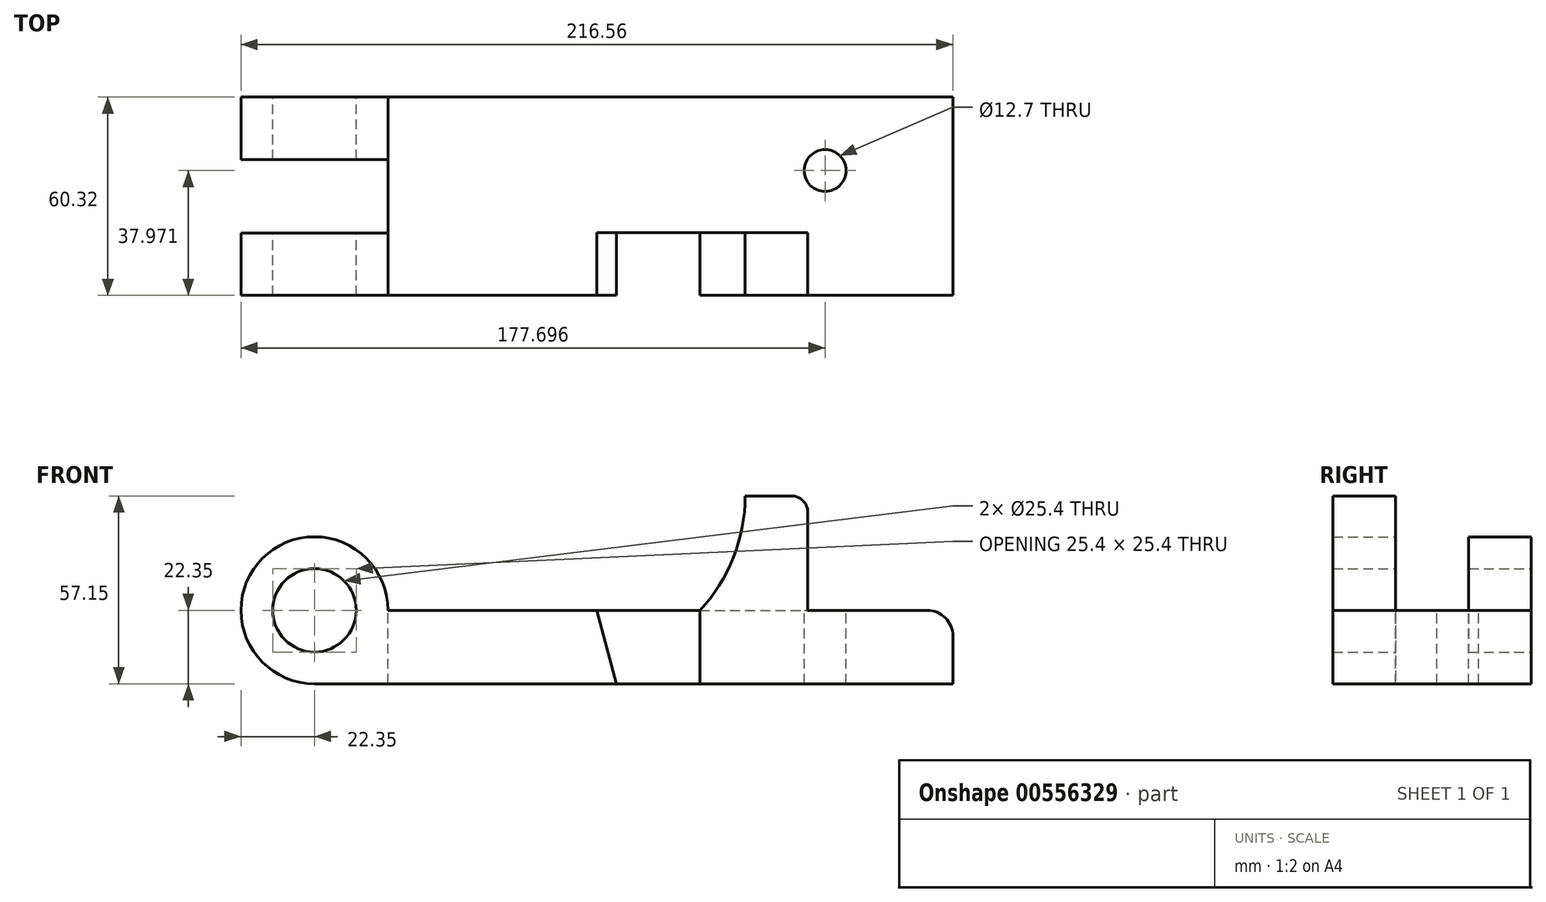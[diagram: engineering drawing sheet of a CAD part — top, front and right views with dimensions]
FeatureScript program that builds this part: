
annotation { "Feature Type Name" : "Feature", "Feature Type Description" : "" }
export const myFeature = defineFeature(function(context is Context, id is Id, definition is map)
    precondition{}
    {
        {
            var Q0;
            Q0=qCreatedBy(makeId("Front.planeOp"),FACE);
            var sketch = newSketch(context, id + "F0", { "sketchPlane" : qUnion([Q0])});
            skCircle(sketch, "E0", {"center": v(0, 0) * mm, "radius": 12.7 * mm});
            skArc(sketch, "E1", {"start": v(22.35, 0) * mm, "mid": v(-15.8, 15.8) * mm, "end": v(0, -22.35) * mm});
            skLineSegment(sketch, "E2.bottom", {"start": v(0, -22.35) * mm, "end": v(194.2, -22.35) * mm});
            skLineSegment(sketch, "E2.top", {"start": v(22.35, 0) * mm, "end": v(194.2, 0) * mm});
            skLineSegment(sketch, "E2.right", {"start": v(194.2, -22.35) * mm, "end": v(194.2, 0) * mm});
            skSolve(sketch);
        }
        {
            var Q0;
            Q0 = qSketchRegion(id + "F0", true);
            extrude(context, id + "F1", {"entities" : qUnion([Q0]), "endBound" : BoundingType.SYMMETRIC, "depth" : 60.32 * mm, "offsetDistance" : 25.4 * mm});
        }
        {
            var Q0;
            Q0=makeQuery(id+"F1.opExtrude","SWEPT_FACE",FACE,{"disambiguationData":[OSD([sQuery(id+"F0.wireOp",EDGE,"E2.top")])]});
            var sketch = newSketch(context, id + "F2", { "sketchPlane" : qUnion([Q0])});
            skLineSegment(sketch, "E3.bottom", {"start": v(22.35, -11.16) * mm, "end": v(-22.52, -11.16) * mm});
            skLineSegment(sketch, "E3.top", {"start": v(22.35, 11.16) * mm, "end": v(-22.52, 11.16) * mm});
            skLineSegment(sketch, "E3.left", {"start": v(22.35, -11.16) * mm, "end": v(22.35, 11.16) * mm});
            skLineSegment(sketch, "E3.right", {"start": v(-22.52, -11.16) * mm, "end": v(-22.52, 11.16) * mm});
            skSolve(sketch);
        }
        {
            var Q0;
            Q0 = qSketchRegion(id + "F2", true);
            extrude(context, id + "F3", {"entities" : qUnion([Q0]), "operationType" : NewBodyOperationType.REMOVE, "endBound" : BoundingType.THROUGH_ALL, "oppositeDirection" : true, "depth" : 25.4 * mm, "offsetDistance" : 25.4 * mm, "hasSecondDirection" : true, "secondDirectionBound" : SecondDirectionBoundingType.THROUGH_ALL, "secondDirectionOppositeDirection" : false, "secondDirectionDepth" : 25.4 * mm});
        }
        {
            var Q0;
            Q0=makeQuery(id+"F1.opExtrude","CAP_FACE",FACE,{"disambiguationData":[OSD([sQuery(id+"F0.wireOp",EDGE,"E0"),sQuery(id+"F0.wireOp",EDGE,"E1"),sQuery(id+"F0.wireOp",EDGE,"E2.bottom"),sQuery(id+"F0.wireOp",EDGE,"E2.top"),sQuery(id+"F0.wireOp",EDGE,"E2.right")])],"isStart":false});
            var sketch = newSketch(context, id + "F4", { "sketchPlane" : qUnion([Q0])});
            skLineSegment(sketch, "E4", {"start": v(85.85, 0) * mm, "end": v(91.85, -22.35) * mm});
            skLineSegment(sketch, "E5", {"start": v(91.85, -22.35) * mm, "end": v(117.25, -22.35) * mm});
            skLineSegment(sketch, "E6", {"start": v(117.25, -22.35) * mm, "end": v(117.25, 0) * mm});
            skSolve(sketch);
        }
        {
            var Q0;
            Q0 = qSketchRegion(id + "F4", true);
            var Q1;
            {var subQ0=sQuery(id+"F4.wireOp",EDGE,"E4");Q1=makeQuery(id+"F4.imprint","IMPRINT",FACE,{"disambiguationData":[TD([[makeQuery(id+"F4.imprint","IMPRINT",EDGE,{"derivedFrom":subQ0}),1.0]])]});}
            extrude(context, id + "F5", {"entities" : qUnion([Q0, Q1]), "operationType" : NewBodyOperationType.REMOVE, "oppositeDirection" : true, "depth" : 19.05 * mm, "offsetDistance" : 25.4 * mm});
        }
        {
            var Q0;
            {var subQ0=sQuery(id+"F0.wireOp",EDGE,"E2.bottom");var subQ1=sQuery(id+"F0.wireOp",EDGE,"E2.top");var subQ2=sQuery(id+"F0.wireOp",EDGE,"E2.right");Q0=makeQuery(id+"F5.boolean.opBoolean","SPLIT",FACE,{"disambiguationData":[TD([makeQuery(id+"F1.opExtrude","SWEPT_FACE",FACE,{"disambiguationData":[OSD([subQ2])]})])],"derivedFrom":makeQuery(id+"F1.opExtrude","CAP_FACE",FACE,{"disambiguationData":[OSD([sQuery(id+"F0.wireOp",EDGE,"E0"),sQuery(id+"F0.wireOp",EDGE,"E1"),subQ0,subQ1,subQ2])],"isStart":false})});}
            var sketch = newSketch(context, id + "F6", { "sketchPlane" : qUnion([Q0])});
            skLineSegment(sketch, "E7", {"start": v(131.04, 34.8) * mm, "end": v(150.09, 34.8) * mm});
            skLineSegment(sketch, "E8", {"start": v(150.09, 34.8) * mm, "end": v(150.09, 0) * mm});
            skLineSegment(sketch, "E9", {"start": v(117.25, 0) * mm, "end": v(150.09, 0) * mm});
            skArc(sketch, "E10", {"start": v(117.25, 0) * mm, "mid": v(127.46, 16.08) * mm, "end": v(131.04, 34.8) * mm});
            skSolve(sketch);
        }
        {
            var Q0;
            Q0 = qSketchRegion(id + "F6", true);
            extrude(context, id + "F7", {"entities" : qUnion([Q0]), "operationType" : NewBodyOperationType.ADD, "oppositeDirection" : true, "depth" : 19.05 * mm, "offsetDistance" : 25.4 * mm});
        }
        {
            var Q0;
            Q0=makeQuery(id+"F1.opExtrude","SWEPT_FACE",FACE,{"disambiguationData":[OSD([sQuery(id+"F0.wireOp",EDGE,"E2.top")])]});
            var sketch = newSketch(context, id + "F8", { "sketchPlane" : qUnion([Q0])});
            skCircle(sketch, "E11", {"center": v(155.35, 7.81) * mm, "radius": 6.35 * mm});
            skSolve(sketch);
        }
        {
            var Q0;
            Q0 = qSketchRegion(id + "F8", true);
            extrude(context, id + "F9", {"entities" : qUnion([Q0]), "operationType" : NewBodyOperationType.REMOVE, "endBound" : BoundingType.THROUGH_ALL, "oppositeDirection" : true, "depth" : 25.4 * mm, "offsetDistance" : 25.4 * mm});
        }
        {
            var Q0;
            Q0=makeQuery(id+"F1.opExtrude","SWEPT_EDGE",EDGE,{"disambiguationData":[OSD([sQuery(id+"F0.wireOp",EDGE,"E2.top"),sQuery(id+"F0.wireOp",EDGE,"E2.right")])]});
            fillet(context, id + "F10", {"entities" : qUnion([Q0]), "radius" : 7.87 * mm, "tangentPropagation" : true, "allowEdgeOverflow" : false});
        }
        {
            var Q0;
            Q0=makeQuery(id+"F7.opExtrude","SWEPT_EDGE",EDGE,{"disambiguationData":[OSD([sQuery(id+"F6.wireOp",EDGE,"E7"),sQuery(id+"F6.wireOp",EDGE,"E8")])]});
            fillet(context, id + "F11", {"entities" : qUnion([Q0]), "radius" : 5.08 * mm, "tangentPropagation" : true, "allowEdgeOverflow" : false});
        }
    });
